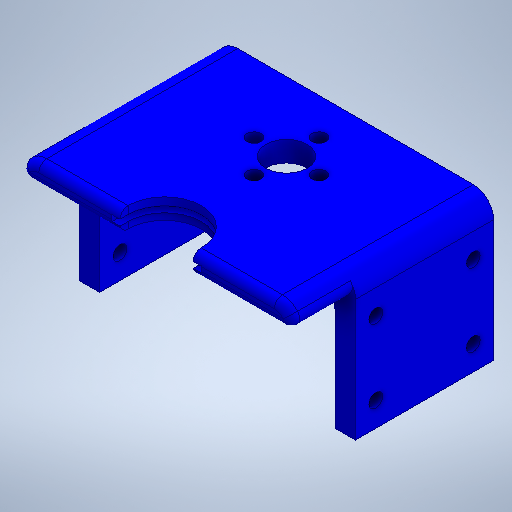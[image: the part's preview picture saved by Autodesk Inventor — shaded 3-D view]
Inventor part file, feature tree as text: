
AUTODESK INVENTOR PART (.ipt)
format: ipt  version: 2025.2 (Build 292293000, 293)  size: 355,840 bytes
history: native  units: mm
features: sketch x7, extrude x5, fillet x3, hole x1
ambient origin geometry x8: Origin, YZ Plane, XZ Plane, XY Plane, X Axis, Y Axis, Z Axis, Center Point
bodies: Solid1 (feature_tree)
feature tree (16):
  extrude  "Extrusion1"  Depth=34.0mm
  extrude  "Extrusion2"  Depth=16.0mm
  hole  "Hole1"  [1 undecoded]
  fillet  "Fillet1"  Radius=5.0mm
  extrude  "Extrusion3"  Depth=5.0mm
  fillet  "Fillet2"  Radius=30.0mm
  fillet  "Fillet3"  Radius=5.0mm
  extrude  "Extrusion4"  Depth=5.0mm
  extrude  "Extrusion5"  Depth=5.0mm
  sketch  "Sketch1"  dims[d0=68.0mm d1=34.0mm]
  sketch  "Sketch Circular Pattern1"  dims[d2=10.2mm d3=16.0mm]
  sketch  "Sketch2"  dims[d4=3.5mm d5=40.0mm d7=360.0deg d9=5.0mm d10=0.0mm]
  sketch  "Sketch3"  dims[d11=5.0mm d12=5.0mm d13=30.0mm d14=0.0mm d15=5.0mm]
  sketch  "Sketch4"  dims[d16=5.0mm d17=6.0mm]
  sketch  "Sketch5"  dims[d18=6.0mm]
  sketch  "Sketch6"  dims[d19=3.4mm d20=6.0mm d21=4.0mm d22=2.0mm d23=90.0deg d24=8.0mm d25=20.594885mm d26=5.0mm d27=15.0mm d28=0.0mm d29=5.0mm d30=2.0mm d31=21.0mm d32=2.0mm d33=18.0mm d34=3.1mm d35=0.0mm d36=22.0mm d37=1.5mm d38=15.0mm d39=0.0mm d40=0.5mm d41=0.872665mm d42=0.5mm d43=0.872665mm]
note: 1 required parameter value undecoded (feature->parameter linkage not recoverable at this tier; creation-order binding heuristic only, values carry confidence <= 0.55)
